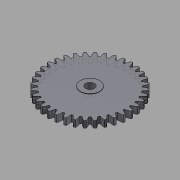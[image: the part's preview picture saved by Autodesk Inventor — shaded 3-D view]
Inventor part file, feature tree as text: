
AUTODESK INVENTOR PART (.ipt)
format: ipt  version: 2015 (Build 190159000, 159)  size: 310,272 bytes
history: native  units: in
note: dims shown in document units (in); Inventor stores cm internally (conversion verified against a paired STEP export)
features: other x13, sketch x4, plane x2
ambient origin geometry x8: Origin, YZ Plane, XZ Plane, XY Plane, X Axis, Y Axis, Z Axis, Center Point
bodies: Solid1 (feature_tree)
feature tree (19):
  other  "Spur Gear2"
  other  "Solid1::Spur Gear2"
  other  "TaggingFeature1"
  sketch  "Sketch1"  dims[d0=0.3937in]
  sketch  "Sketch2"  dims[d16=0.4528in d17=0.0in d41=0.0in d43=0.4528in d46=0.4528in d47=0.0in d48=0.0in]
  sketch  "Sketch3"
  sketch  "Sketch4"
  plane  "XZ Plane_1"
  plane  "Work Plane2"
  other  "Z Axis_1"
  other  "Srf1"
  other  "Srf1::Derived"
  other  "Distance iMate"
  other  "Align iMate"
  other  "Mesh iMate"
  other  "Axis iMate"
  other  "Position iMate"
  other  "Mesh iMate2"
  other  "Start plane iMate"
